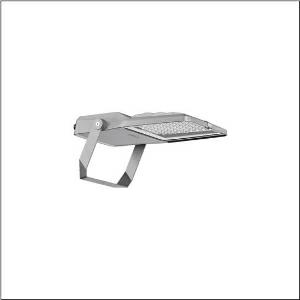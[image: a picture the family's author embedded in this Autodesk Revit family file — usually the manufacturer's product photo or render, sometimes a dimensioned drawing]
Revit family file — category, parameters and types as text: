
# Revit family: floodlight_fl_21_iq_mini___rs12_5xa7772d2b1a_9233
name_source: partatom
category: Lighting Fixtures
units: mm (PartAtom-declared; Revit-internal decimal feet)

## family parameters
Cut with Voids When Loaded = No
Host = Face
Light Source = No
Part Type = Normal
Room Calculation Point = No
Round Connector Dimension = Use Diameter
Shared = No

## types (1)
- --- (1 x LED, 18020 lm, 143 W, 3000K)
    Apparent Load = 143 VA
    CIE Flux Codes = 79 92 99 100 100
    Color Rendering = 70
    Color Temperature = 3000K
    Default Elevation = 1800 mm
    Description = Floodlight FL 21 iQ mini, floodlight, primary light control with lens, of PMMA, primary optical cover: protective disc, of toughened safety glass, transparent, light distribution: RS12, light emission: direct distribution, installation type: surface-mounted, LED, High Power LED, rated luminous flux: 18.020lm, luminous efficacy: 126lm/W, light colour: 730, colour temperature: 3000K, control gear: iQ Street-Remote/DALI, control: Street-Remote, Auto-Match, Temp-Guard, Night-Set, Smart-Wire, Desk-Remote (wireless, voltage-free reading and setting of iQ features in the workshop via application-optimized NFC function/RFID function), optimised constant luminous flux control (CLO 2.0), with terminal, 6-pole, mains connection: 220..240V, AC, 50/60Hz, start of lifetime: 143W, end of service life: 152W, reduction: 61W, luminaire housing, of diecast aluminium, powder-coated, Siteco® metallic grey (DB 702S), corrosivity category C5 mid according to DIN EN ISO 12944, suitable for swimming pools, chlorine-resistant, sealing non-destructively replaceable, mounting bracket, of steel, galvanised, powder-coated, Siteco® metallic grey (DB 702S), protection rating (complete): IP66, insulation class (complete): insulation class II (safety insulation), certification: CE, ENEC, VDE, protection symbol: D, impact resistance: IK08, permissible operating ambient temperature: -40..+40°C, permissible operating ambient temperature for outdoor applications: -40..+50°C, standard: DIN EN 12944, LABS conformity tested according to VDMA 24364:2018-05, packaging unit: 1 piece

Light Distribution: RS12
    Height = 70 mm
    Lamp = 1 x LED
    Lamp Light Flux = 18020 lm
    Lamp Power = 143 W
    Lamp count = 1
    Length = 485 mm
    Luminous efficacy = 126 lm/W
    Manufacturer = Siteco
    ModVariant = No
    Model = 5XA7772D2B1A
    Number of Poles = 1
    OnlyDefault = Yes
    Power Factor = 1
    Product Name = Floodlight FL 21 iQ mini | RS12
    Product group = floodlight | pylon annexe
    ProductGroupID = 6201
    Protection Class = Protection class II
    Protection Degree = IP 66
    RLX_Detail_Level = 1
    RLX_Emergency_Light_Flux = 0 lm
    RLX_Emergency_Type = 0
    RLX_Emergency_Type_DB = No
    RlxData = <blob elided: 91385 chars, md5=25a244c5>
    Socket = socket
    Standby Power = 0 W
    System Light Flux = 18020 lm
    System Power = 143 W
    Type Comments = factory setting: luminous flux: 100 % | dim-lin: 254 | 730 mA
    Type Image = l_1006845.jpg
    URL = http://relux.com
    VarID = @adj_188841
    Voltage = 0 V
    Weight = 0.00 kg
    Width = 337 mm

## geometry (parser evidence)
native form markers: Blend x4, Sweep x13
no freeform markers — native parametric forms only
